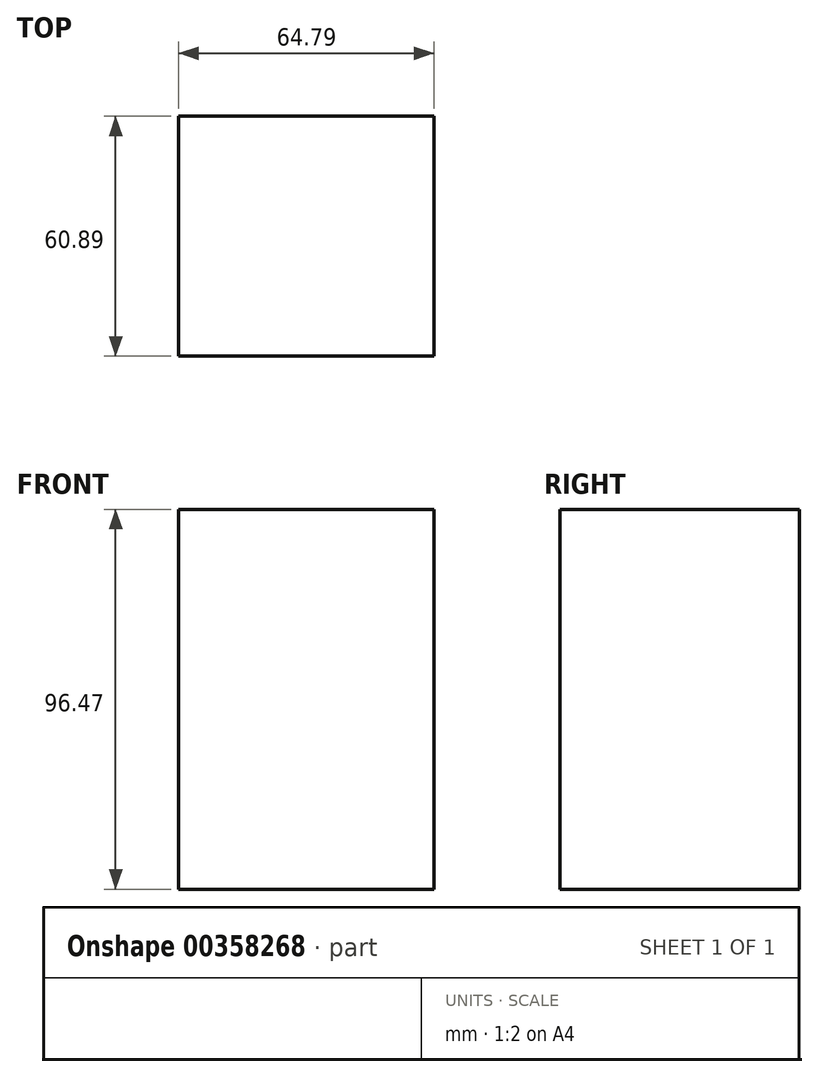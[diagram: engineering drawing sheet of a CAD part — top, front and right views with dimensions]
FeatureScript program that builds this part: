
annotation { "Feature Type Name" : "Feature", "Feature Type Description" : "" }
export const myFeature = defineFeature(function(context is Context, id is Id, definition is map)
    precondition{}
    {
        {
            var Q0;
            Q0=qCreatedBy(makeId("Top.planeOp"),FACE);
            var sketch = newSketch(context, id + "F0", { "sketchPlane" : qUnion([Q0])});
            skLineSegment(sketch, "E0.bottom", {"start": v(0, 39.74) * mm, "end": v(64.8, 39.74) * mm});
            skLineSegment(sketch, "E0.top", {"start": v(0, -21.15) * mm, "end": v(64.8, -21.15) * mm});
            skLineSegment(sketch, "E0.left", {"start": v(0, 39.74) * mm, "end": v(0, -21.15) * mm});
            skLineSegment(sketch, "E0.right", {"start": v(64.8, 39.74) * mm, "end": v(64.8, -21.15) * mm});
            skSolve(sketch);
        }
        {
            var Q0;
            Q0 = qSketchRegion(id + "F0", true);
            extrude(context, id + "F1", {"entities" : qUnion([Q0]), "depth" : 96.47 * mm});
        }
    });
